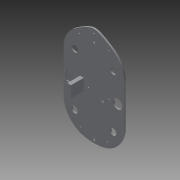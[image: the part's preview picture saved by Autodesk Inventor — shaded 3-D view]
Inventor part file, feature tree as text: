
AUTODESK INVENTOR PART (.ipt)
format: ipt  version: 2014 (Build 180170000, 170)  size: 497,664 bytes
history: native  units: mm
features: extrude x18, sketch x17, projected_geometry x8, fillet x3, other x1
ambient origin geometry x8: Origin, YZ Plane, XZ Plane, XY Plane, X Axis, Y Axis, Z Axis, Center Point
bodies: Body1 (feature_tree)
feature tree (47):
  other  "ソリッド1"
  extrude  "押し出し1"  Depth=115.0mm
  extrude  "押し出し4"  Depth=130.0mm
  extrude  "押し出し5"  Depth=65.0mm
  extrude  "押し出し6"  Depth=57.5mm
  fillet  "フィレット1"  Radius=3.0mm
  extrude  "押し出し7"  Depth=12.2mm
  extrude  "押し出し8"  Depth=12.2mm
  extrude  "押し出し9"  Depth=12.2mm
  extrude  "押し出し10"  Depth=12.2mm
  extrude  "押し出し13"  Depth=21.0mm
  extrude  "押し出し14"  Depth=21.0mm
  fillet  "フィレット2"  Radius=15.0mm
  extrude  "押し出し15"  Depth=15.0mm
  fillet  "フィレット3"  Radius=15.0mm
  extrude  "押し出し16"  Depth=15.0mm
  extrude  "押し出し17"  Depth=21.0mm
  extrude  "押し出し18"  Depth=21.0mm
  extrude  "押し出し19"  Depth=3.0mm TaperAngle=0.0deg
  extrude  "押し出し20"  TaperAngle=0.0deg  [1 undecoded]
  extrude  "押し出し21"  Depth=30.0mm
  extrude  "押し出し22"  Depth=17.0mm
  sketch  "スケッチ1"
  sketch  "スケッチ2"
  sketch  "スケッチ4"
  sketch  "スケッチ7"
  sketch  "スケッチ8"
  projected_geometry  "投影ループ1"
  sketch  "スケッチ9"
  sketch  "スケッチ10"
  projected_geometry  "投影ループ2"
  sketch  "スケッチ11"
  projected_geometry  "投影ループ3"
  projected_geometry  "投影ループ4"
  sketch  "スケッチ14"
  sketch  "スケッチ15"
  projected_geometry  "投影ループ6"
  sketch  "スケッチ16"
  projected_geometry  "投影ループ7"
  sketch  "スケッチ17"
  projected_geometry  "投影ループ8"
  projected_geometry  "投影ループ10"
  sketch  "スケッチ20"
  sketch  "スケッチ21"
  sketch  "スケッチ22"
  sketch  "スケッチ23"
  sketch  "スケッチ24"
note: 1 required parameter value undecoded (feature->parameter linkage not recoverable at this tier; creation-order binding heuristic only, values carry confidence <= 0.55)
